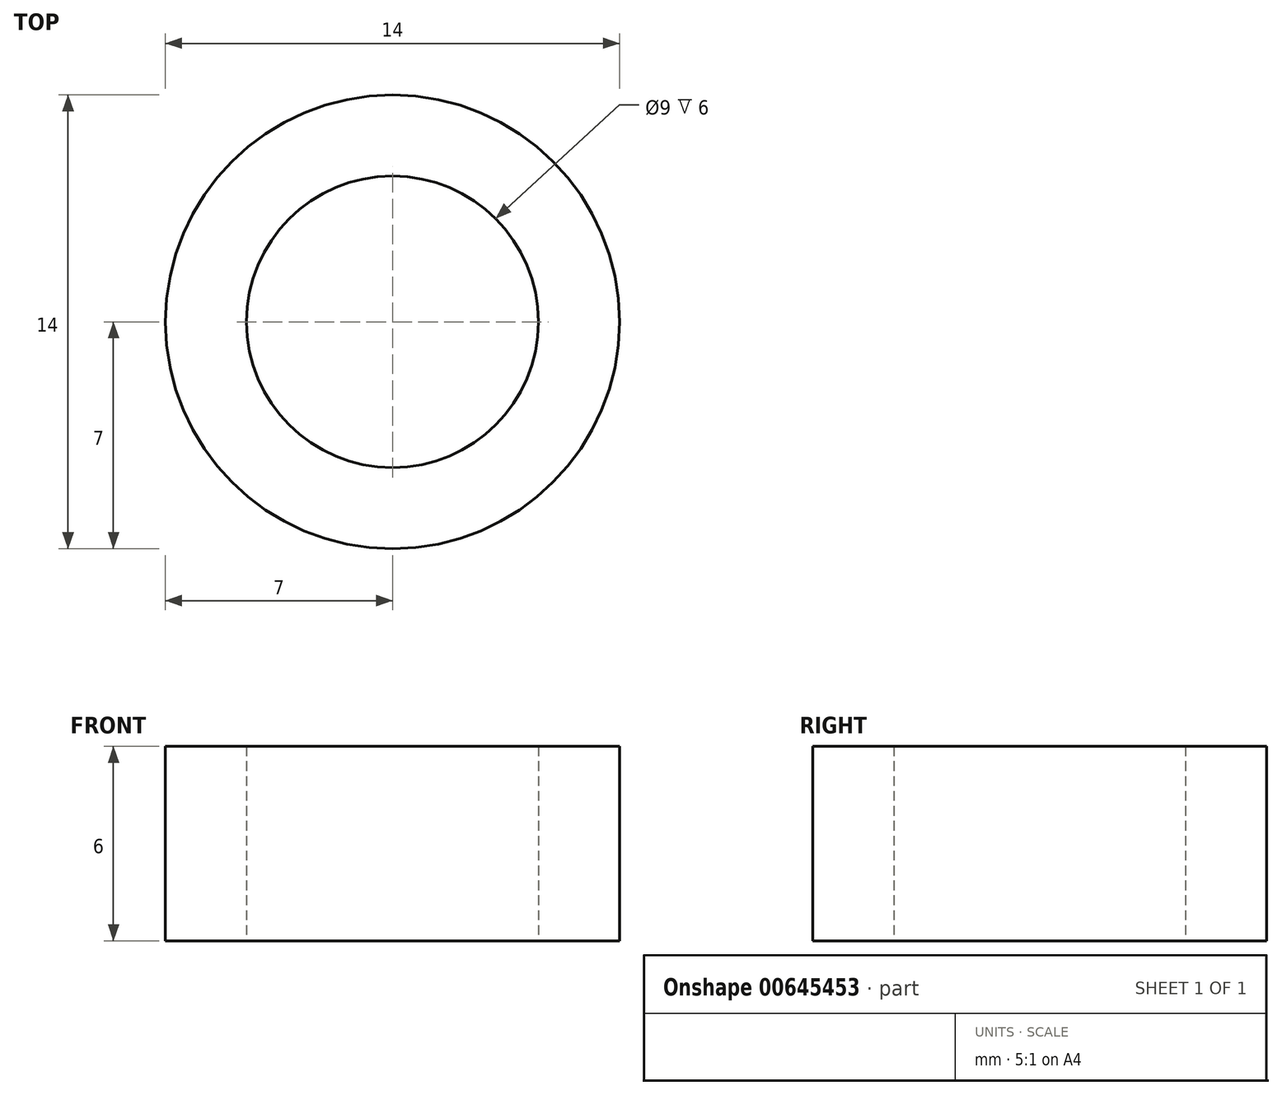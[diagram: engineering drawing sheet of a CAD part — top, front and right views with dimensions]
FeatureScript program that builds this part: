
annotation { "Feature Type Name" : "Feature", "Feature Type Description" : "" }
export const myFeature = defineFeature(function(context is Context, id is Id, definition is map)
    precondition{}
    {
        {
            var Q0;
            Q0=qCreatedBy(makeId("Top.planeOp"),FACE);
            var sketch = newSketch(context, id + "F0", { "sketchPlane" : qUnion([Q0])});
            skCircle(sketch, "E0", {"center": v(0, 0) * mm, "radius": 7 * mm});
            skCircle(sketch, "E1", {"center": v(0, 0) * mm, "radius": 4.5 * mm});
            skSolve(sketch);
        }
        {
            var Q0;
            Q0=makeQuery(id+"F0.imprint","IMPRINT",FACE,{"disambiguationData":[TD([[makeQuery(id+"F0.imprint","IMPRINT",EDGE,{"derivedFrom":sQuery(id+"F0.wireOp",EDGE,"E0")}),1.0]])]});
            extrude(context, id + "F1", {"entities" : qUnion([Q0]), "depth" : 6 * mm, "offsetDistance" : 25 * mm});
        }
    });
